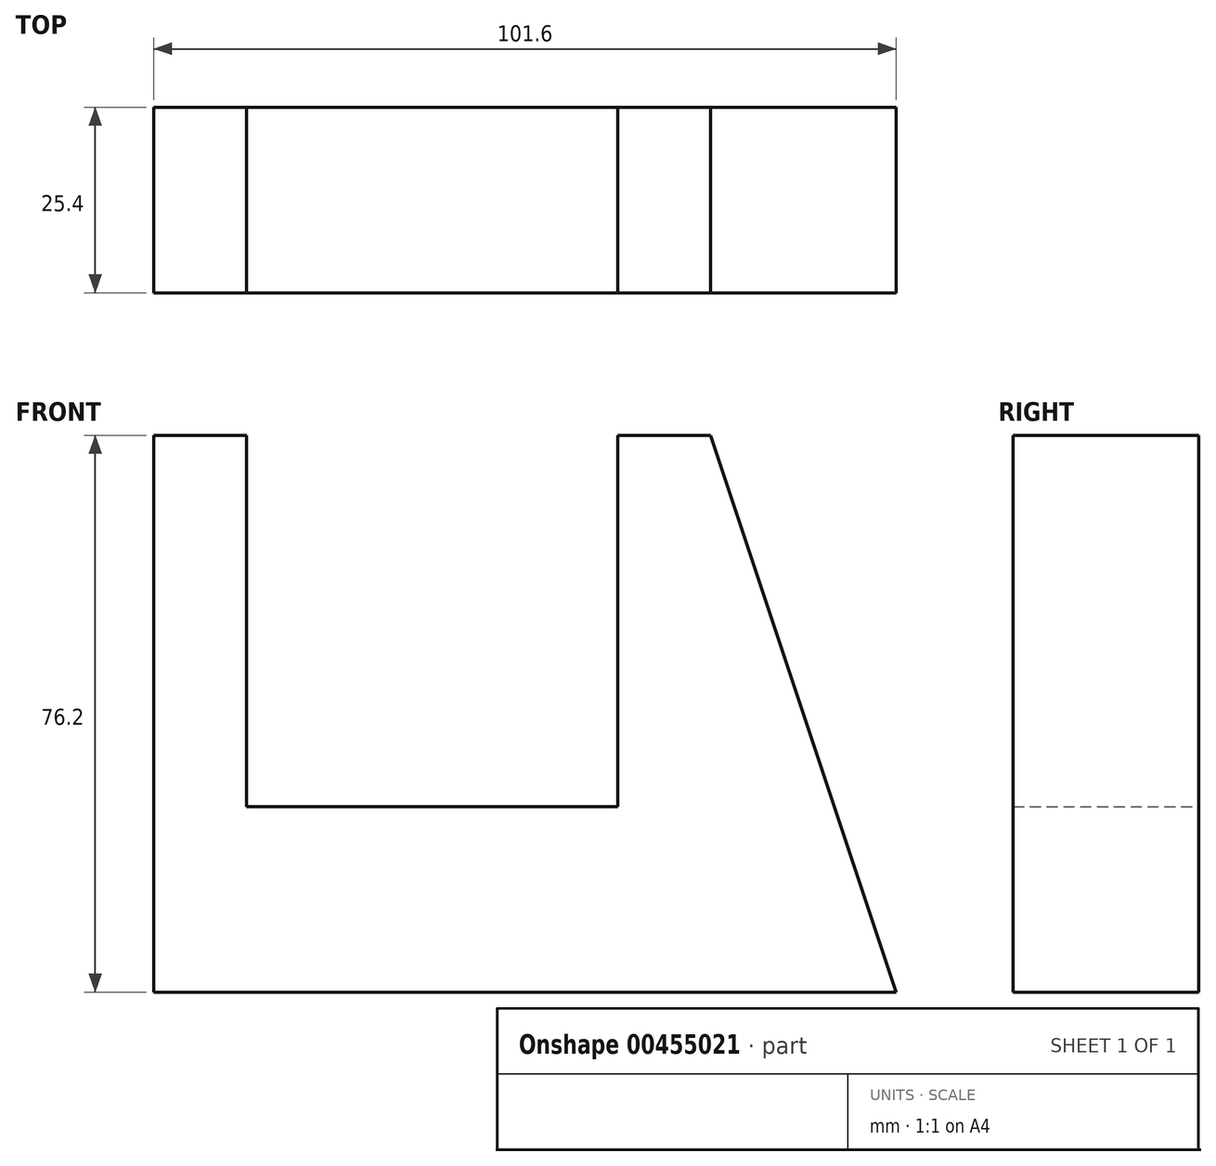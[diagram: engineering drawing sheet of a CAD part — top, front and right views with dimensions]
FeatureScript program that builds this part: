
annotation { "Feature Type Name" : "Feature", "Feature Type Description" : "" }
export const myFeature = defineFeature(function(context is Context, id is Id, definition is map)
    precondition{}
    {
        {
            var Q0;
            Q0=qCreatedBy(makeId("Front.planeOp"),FACE);
            var sketch = newSketch(context, id + "F0", { "sketchPlane" : qUnion([Q0])});
            skLineSegment(sketch, "E0", {"start": v(59.67, 0) * mm, "end": v(-16.53, 0) * mm});
            skLineSegment(sketch, "E1", {"start": v(-16.53, 0) * mm, "end": v(-16.53, 76.2) * mm});
            skLineSegment(sketch, "E2", {"start": v(-16.53, 76.2) * mm, "end": v(-3.83, 76.2) * mm});
            skLineSegment(sketch, "E3", {"start": v(-3.83, 76.2) * mm, "end": v(-3.83, 25.4) * mm});
            skLineSegment(sketch, "E4", {"start": v(-3.83, 25.4) * mm, "end": v(46.97, 25.4) * mm});
            skLineSegment(sketch, "E5", {"start": v(46.97, 25.4) * mm, "end": v(46.97, 76.2) * mm});
            skLineSegment(sketch, "E6", {"start": v(46.97, 76.2) * mm, "end": v(59.67, 76.2) * mm});
            skLineSegment(sketch, "E7", {"start": v(59.67, 76.2) * mm, "end": v(85.07, 0) * mm});
            skLineSegment(sketch, "E8", {"start": v(85.07, 0) * mm, "end": v(59.67, 0) * mm});
            skSolve(sketch);
        }
        {
            var Q0;
            Q0 = qSketchRegion(id + "F0", true);
            extrude(context, id + "F1", {"entities" : qUnion([Q0]), "depth" : 25.4 * mm, "offsetDistance" : 25.4 * mm});
        }
    });
